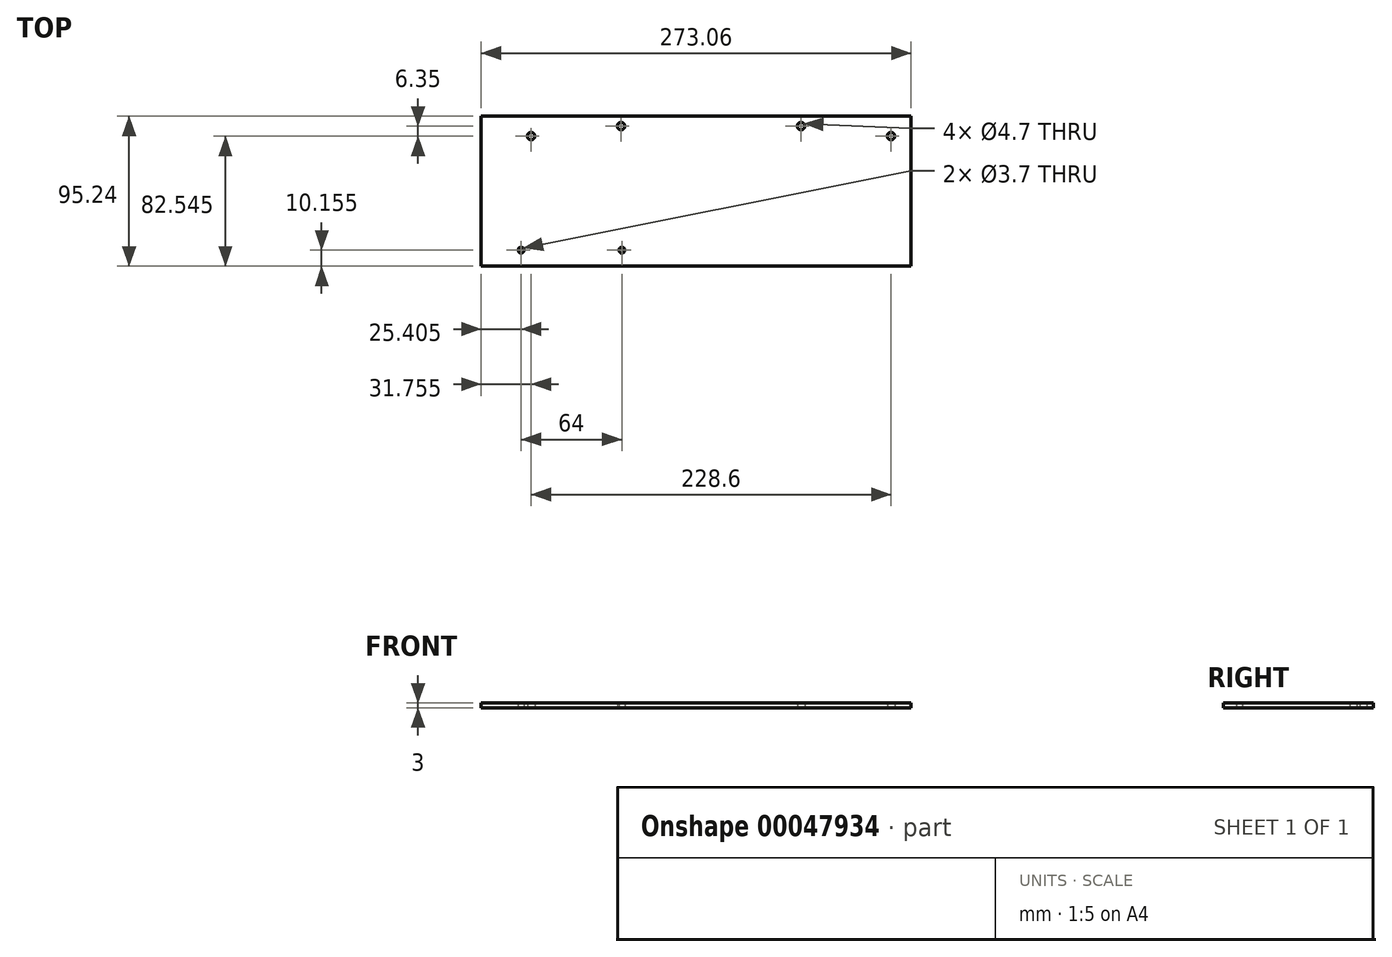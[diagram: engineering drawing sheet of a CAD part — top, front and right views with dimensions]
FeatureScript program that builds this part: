
annotation { "Feature Type Name" : "Feature", "Feature Type Description" : "" }
export const myFeature = defineFeature(function(context is Context, id is Id, definition is map)
    precondition{}
    {
        {
            var Q0;
            Q0=qCreatedBy(makeId("Top.planeOp"),FACE);
            var sketch = newSketch(context, id + "F0", { "sketchPlane" : qUnion([Q0])});
            skLineSegment(sketch, "E0.rect.bottom", {"start": v(-136.53, -47.63) * mm, "end": v(136.53, -47.63) * mm});
            skLineSegment(sketch, "E0.rect.top", {"start": v(-136.53, 47.63) * mm, "end": v(136.53, 47.63) * mm});
            skLineSegment(sketch, "E0.rect.left", {"start": v(-136.53, -47.63) * mm, "end": v(-136.53, 47.63) * mm});
            skLineSegment(sketch, "E0.rect.right", {"start": v(136.53, -47.63) * mm, "end": v(136.53, 47.63) * mm});
            skPoint(sketch, "E0.rect.middle", {"position": v(0, 0) * mm});
            skLineSegment(sketch, "E1.bottom", {"start": v(-136.53, 47.63) * mm, "end": v(-123.83, 47.63) * mm, "construction": true});
            skLineSegment(sketch, "E1.left", {"start": v(-136.53, 47.63) * mm, "end": v(-136.53, 34.92) * mm, "construction": true});
            skLineSegment(sketch, "E2.bottom", {"start": v(136.53, 47.63) * mm, "end": v(123.83, 47.63) * mm, "construction": true});
            skLineSegment(sketch, "E2.top", {"start": v(136.52, 34.93) * mm, "end": v(123.82, 34.93) * mm, "construction": true});
            skLineSegment(sketch, "E2.left", {"start": v(136.53, 47.63) * mm, "end": v(136.53, 34.93) * mm, "construction": true});
            skLineSegment(sketch, "E2.right", {"start": v(123.83, 47.63) * mm, "end": v(123.83, 34.93) * mm, "construction": true});
            skCircle(sketch, "E3", {"center": v(123.82, 34.93) * mm, "radius": 2.35 * mm});
            skLineSegment(sketch, "E4", {"start": v(123.82, 34.92) * mm, "end": v(-104.78, 34.92) * mm, "construction": true});
            skLineSegment(sketch, "E5", {"start": v(9.52, 34.92) * mm, "end": v(9.52, 41.27) * mm, "construction": true});
            skLineSegment(sketch, "E6", {"start": v(9.52, 41.27) * mm, "end": v(66.68, 41.27) * mm, "construction": true});
            skCircle(sketch, "E7", {"center": v(66.68, 41.27) * mm, "radius": 2.35 * mm});
            skLineSegment(sketch, "E8", {"start": v(9.52, 41.27) * mm, "end": v(-47.63, 41.27) * mm, "construction": true});
            skCircle(sketch, "E9", {"center": v(-47.63, 41.27) * mm, "radius": 2.35 * mm});
            skCircle(sketch, "E10", {"center": v(-104.78, 34.92) * mm, "radius": 2.35 * mm});
            skLineSegment(sketch, "E11.bottom", {"start": v(-136.53, -47.63) * mm, "end": v(-111.12, -47.63) * mm, "construction": true});
            skLineSegment(sketch, "E11.top", {"start": v(-136.53, -37.47) * mm, "end": v(-111.12, -37.47) * mm, "construction": true});
            skLineSegment(sketch, "E11.left", {"start": v(-136.53, -47.63) * mm, "end": v(-136.53, -37.47) * mm, "construction": true});
            skLineSegment(sketch, "E11.right", {"start": v(-111.12, -47.63) * mm, "end": v(-111.12, -37.47) * mm, "construction": true});
            skCircle(sketch, "E12", {"center": v(-111.12, -37.47) * mm, "radius": 1.85 * mm});
            skLineSegment(sketch, "E13", {"start": v(-111.12, -37.47) * mm, "end": v(-47.12, -37.47) * mm, "construction": true});
            skCircle(sketch, "E14", {"center": v(-47.12, -37.47) * mm, "radius": 1.85 * mm});
            skSolve(sketch);
        }
        {
            var Q0;
            Q0=makeQuery(id+"F0.imprint","IMPRINT",FACE,{"disambiguationData":[TD([[makeQuery(id+"F0.imprint","IMPRINT",EDGE,{"derivedFrom":sQuery(id+"F0.wireOp",EDGE,"E0.rect.bottom")}),1.0]])]});
            extrude(context, id + "F1", {"entities" : qUnion([Q0]), "depth" : 3 * mm});
        }
    });
